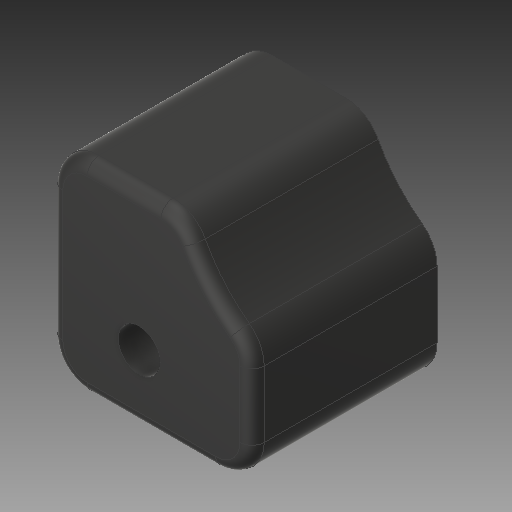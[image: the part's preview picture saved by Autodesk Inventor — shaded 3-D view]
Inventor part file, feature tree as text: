
AUTODESK INVENTOR PART (.ipt)
format: ipt  version: 2018 (Build 220112000, 112)  size: 195,584 bytes
history: native  units: in
note: dims shown in document units (in); Inventor stores cm internally (conversion verified against a paired STEP export)
features: sketch x3, extrude x3, plane x1, fillet x1, projected_geometry x1
ambient origin geometry x8: Origin, YZ Plane, XZ Plane, XY Plane, X Axis, Y Axis, Z Axis, Center Point
bodies: Solid1 (feature_tree)
feature tree (9):
  sketch  "Sketch1"  dims[d0=0.1181in d1=0.1181in d2=1.0in d3=0.0in]
  plane  "Work Plane1"
  extrude  "Extrusion1"  Depth=0.1181in TaperAngle=0.0deg
  extrude  "Extrusion2"  Depth=0.0787in TaperAngle=0.0deg
  extrude  "Extrusion3"  Depth=0.0394in
  fillet  "Fillet1"  Radius=0.0787in
  sketch  "Sketch2"  dims[d4=0.0197in d5=0.0787in d6=0.0in]
  projected_geometry  "Projected Loop1"
  sketch  "Sketch3"  dims[d7=0.2085in d8=0.315in d9=0.0787in d10=0.0in d11=0.0394in]
